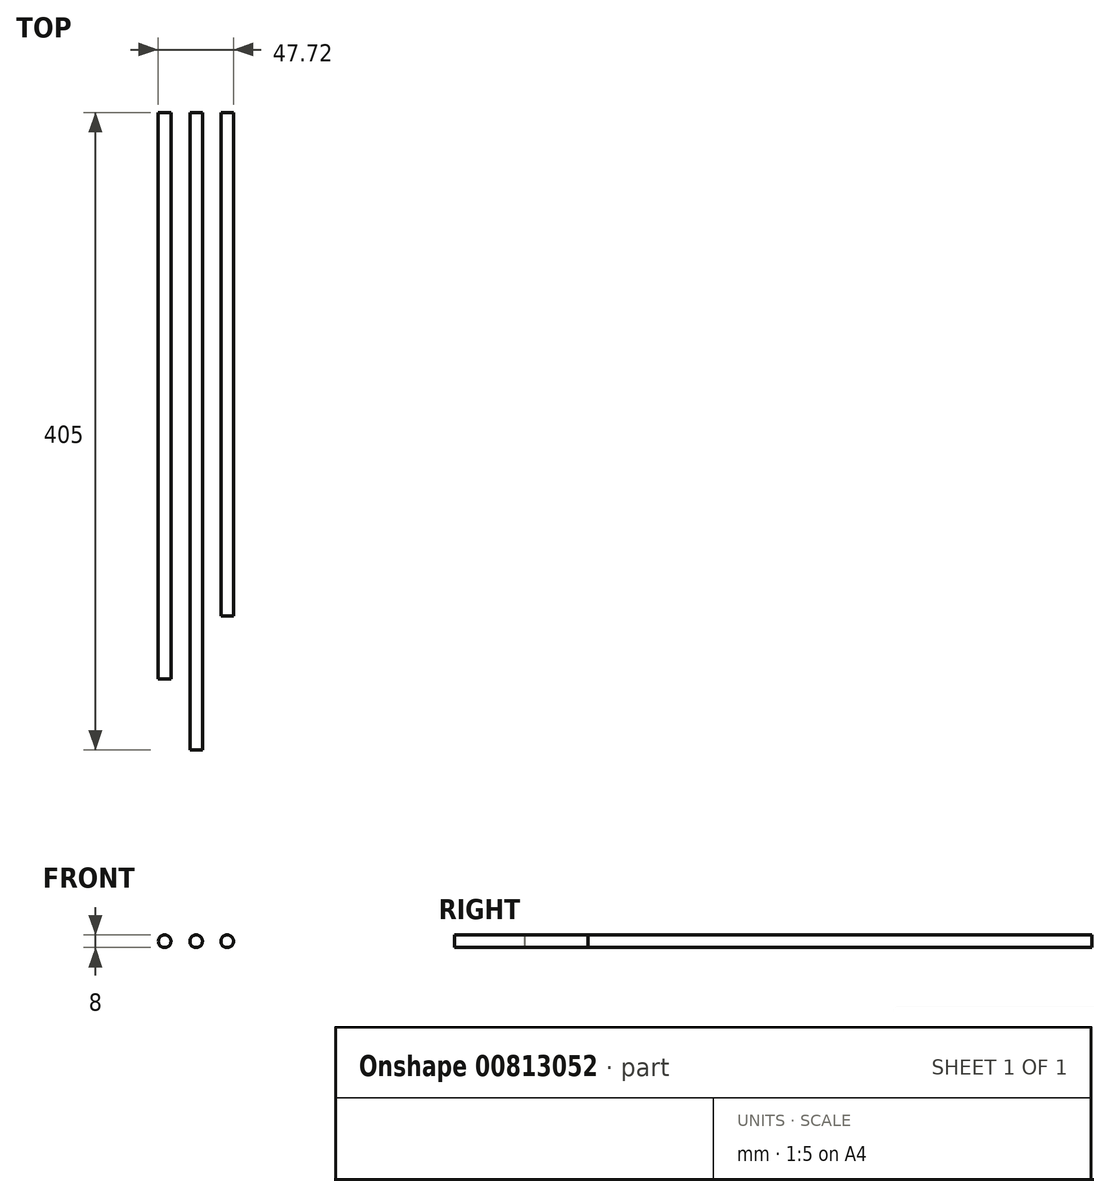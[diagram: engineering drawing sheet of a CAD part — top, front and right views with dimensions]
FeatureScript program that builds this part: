
annotation { "Feature Type Name" : "Feature", "Feature Type Description" : "" }
export const myFeature = defineFeature(function(context is Context, id is Id, definition is map)
    precondition{}
    {
        {
            var Q0;
            Q0=qCreatedBy(makeId("Front.planeOp"),FACE);
            var sketch = newSketch(context, id + "F0", { "sketchPlane" : qUnion([Q0])});
            skCircle(sketch, "E0", {"center": v(0, 0) * mm, "radius": 4 * mm});
            skSolve(sketch);
        }
        {
            var Q0;
            Q0=qSketchRegion(id+"F0",true);
            extrude(context, id + "F1", {"entities" : qUnion([Q0]), "depth" : 360 * mm, "offsetDistance" : 25 * mm});
        }
        {
            var Q0;
            Q0=qCreatedBy(makeId("Front.planeOp"),FACE);
            var sketch = newSketch(context, id + "F2", { "sketchPlane" : qUnion([Q0])});
            skCircle(sketch, "E1", {"center": v(20.01, 0) * mm, "radius": 4 * mm});
            skSolve(sketch);
        }
        {
            var Q0;
            Q0=makeQuery(id+"F2.imprint","IMPRINT",FACE,{"disambiguationData":[TD([[makeQuery(id+"F2.imprint","IMPRINT",EDGE,{"derivedFrom":sQuery(id+"F2.wireOp",EDGE,"E1")}),1.0]])]});
            extrude(context, id + "F3", {"entities" : qUnion([Q0]), "depth" : 405 * mm, "offsetDistance" : 25 * mm});
        }
        {
            var Q0;
            Q0=qCreatedBy(makeId("Front.planeOp"),FACE);
            var sketch = newSketch(context, id + "F4", { "sketchPlane" : qUnion([Q0])});
            skCircle(sketch, "E2", {"center": v(39.72, 0) * mm, "radius": 4 * mm});
            skSolve(sketch);
        }
        {
            var Q0;
            Q0=makeQuery(id+"F4.imprint","IMPRINT",FACE,{"disambiguationData":[TD([[makeQuery(id+"F4.imprint","IMPRINT",EDGE,{"derivedFrom":sQuery(id+"F4.wireOp",EDGE,"E2")}),1.0]])]});
            extrude(context, id + "F5", {"entities" : qUnion([Q0]), "depth" : 320 * mm, "offsetDistance" : 25 * mm});
        }
    });
